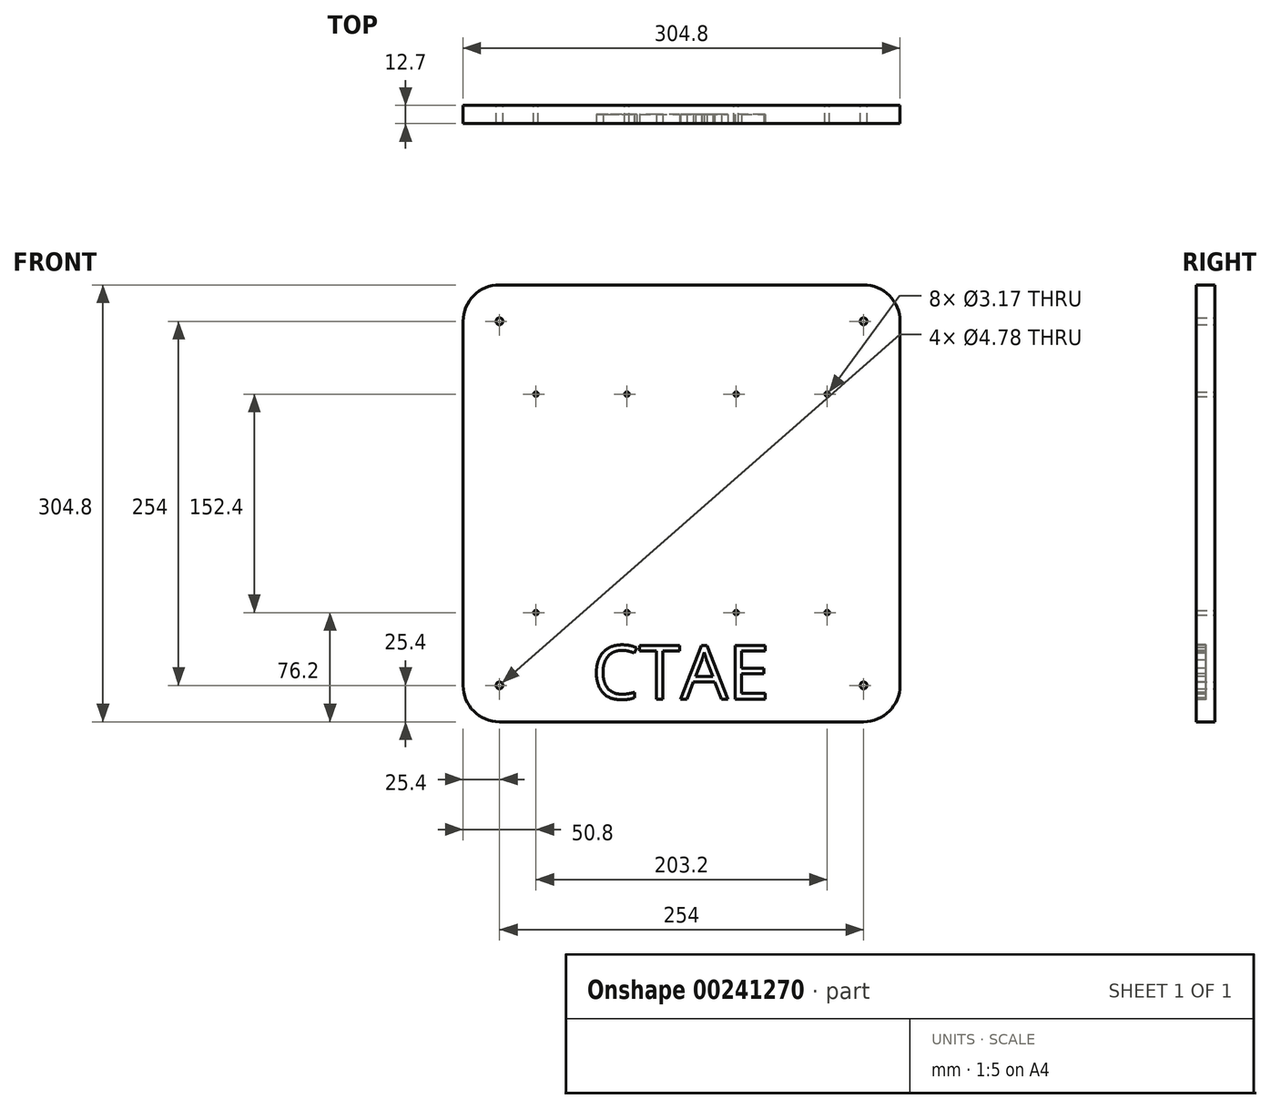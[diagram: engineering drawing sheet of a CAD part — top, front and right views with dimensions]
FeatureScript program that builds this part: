
annotation { "Feature Type Name" : "Feature", "Feature Type Description" : "" }
export const myFeature = defineFeature(function(context is Context, id is Id, definition is map)
    precondition{}
    {
        {
            var Q0;
            Q0=qCreatedBy(makeId("Front.planeOp"),FACE);
            var sketch = newSketch(context, id + "F0", { "sketchPlane" : qUnion([Q0])});
            skLineSegment(sketch, "E0.bottom", {"start": v(25.4, 0) * mm, "end": v(279.4, 0) * mm});
            skLineSegment(sketch, "E0.top", {"start": v(25.4, 304.8) * mm, "end": v(279.4, 304.8) * mm});
            skLineSegment(sketch, "E0.left", {"start": v(0, 25.4) * mm, "end": v(0, 279.4) * mm});
            skLineSegment(sketch, "E0.right", {"start": v(304.8, 25.4) * mm, "end": v(304.8, 279.4) * mm});
            skPoint(sketch, "E1.visualSharp", {"position": v(0, 304.8) * mm});
            skArc(sketch, "E1.filletArc", {"start": v(25.4, 304.8) * mm, "mid": v(7.44, 297.36) * mm, "end": v(0, 279.4) * mm});
            skPoint(sketch, "E2.visualSharp", {"position": v(304.8, 304.8) * mm});
            skArc(sketch, "E2.filletArc", {"start": v(304.8, 279.4) * mm, "mid": v(297.36, 297.36) * mm, "end": v(279.4, 304.8) * mm});
            skPoint(sketch, "E3.visualSharp", {"position": v(304.8, 0) * mm});
            skArc(sketch, "E3.filletArc", {"start": v(279.4, 0) * mm, "mid": v(297.36, 7.44) * mm, "end": v(304.8, 25.4) * mm});
            skPoint(sketch, "E4.visualSharp", {"position": v(0, 0) * mm});
            skArc(sketch, "E4.filletArc", {"start": v(0, 25.4) * mm, "mid": v(7.44, 7.44) * mm, "end": v(25.4, 0) * mm});
            skLineSegment(sketch, "E5", {"start": v(0, 152.4) * mm, "end": v(304.8, 152.4) * mm, "construction": true});
            skPoint(sketch, "E6", {"position": v(50.8, 228.6) * mm});
            skPoint(sketch, "E7", {"position": v(114.3, 228.6) * mm});
            skPoint(sketch, "E8", {"position": v(190.5, 228.6) * mm});
            skPoint(sketch, "E9", {"position": v(254, 228.6) * mm});
            skPoint(sketch, "E10.MirrorP", {"position": v(50.8, 76.2) * mm});
            skPoint(sketch, "E11.MirrorP", {"position": v(114.3, 76.2) * mm});
            skPoint(sketch, "E12.MirrorP", {"position": v(190.5, 76.2) * mm});
            skPoint(sketch, "E13.MirrorP", {"position": v(254, 76.2) * mm});
            skSolve(sketch);
        }
        {
            var Q0;
            Q0=makeQuery(id+"F0.imprint","IMPRINT",FACE,{"disambiguationData":[TD([[makeQuery(id+"F0.imprint","IMPRINT",EDGE,{"derivedFrom":sQuery(id+"F0.wireOp",EDGE,"E0.bottom")}),1.0]])]});
            extrude(context, id + "F1", {"entities" : qUnion([Q0]), "depth" : 12.7 * mm});
        }
        {
            var Q0;
            Q0=sQuery(id+"F0.wireOp",VERTEX,"E1.filletArc.center");
            var Q1;
            Q1=sQuery(id+"F0.wireOp",VERTEX,"E4.filletArc.center");
            var Q2;
            Q2=sQuery(id+"F0.wireOp",VERTEX,"E3.filletArc.center");
            var Q3;
            Q3=sQuery(id+"F0.wireOp",VERTEX,"E2.filletArc.center");
            var Q4;
            Q4=makeQuery(id+"F1.opExtrude","SWEPT_BODY",BODY,{"disambiguationData":[OSD([sQuery(id+"F0.wireOp",EDGE,"E0.bottom"),sQuery(id+"F0.wireOp",EDGE,"E0.top"),sQuery(id+"F0.wireOp",EDGE,"E0.left"),sQuery(id+"F0.wireOp",EDGE,"E0.right"),sQuery(id+"F0.wireOp",EDGE,"E1.filletArc"),sQuery(id+"F0.wireOp",EDGE,"E2.filletArc"),sQuery(id+"F0.wireOp",EDGE,"E3.filletArc"),sQuery(id+"F0.wireOp",EDGE,"E4.filletArc")])]});
            hole(context, id + "F2", {"style" : HoleStyle.SIMPLE, "endStyle" : HoleEndStyle.THROUGH, "oppositeDirection" : true, "holeDiameter" : 4.78 * mm, "locations" : qUnion([Q0, Q1, Q2, Q3]), "scope" : qUnion([Q4]), "isTappedThrough" : true});
        }
        {
            var Q0;
            Q0=sQuery(id+"F0.wireOp",VERTEX,"E6");
            var Q1;
            Q1=sQuery(id+"F0.wireOp",VERTEX,"E7");
            var Q2;
            Q2=sQuery(id+"F0.wireOp",VERTEX,"E8");
            var Q3;
            Q3=sQuery(id+"F0.wireOp",VERTEX,"E9");
            var Q4;
            Q4=sQuery(id+"F0.wireOp",VERTEX,"E13.MirrorP");
            var Q5;
            Q5=sQuery(id+"F0.wireOp",VERTEX,"E12.MirrorP");
            var Q6;
            Q6=sQuery(id+"F0.wireOp",VERTEX,"E10.MirrorP");
            var Q7;
            Q7=sQuery(id+"F0.wireOp",VERTEX,"E11.MirrorP");
            var Q8;
            Q8=makeQuery(id+"F1.opExtrude","SWEPT_BODY",BODY,{"disambiguationData":[OSD([sQuery(id+"F0.wireOp",EDGE,"E0.bottom"),sQuery(id+"F0.wireOp",EDGE,"E0.top"),sQuery(id+"F0.wireOp",EDGE,"E0.left"),sQuery(id+"F0.wireOp",EDGE,"E0.right"),sQuery(id+"F0.wireOp",EDGE,"E1.filletArc"),sQuery(id+"F0.wireOp",EDGE,"E2.filletArc"),sQuery(id+"F0.wireOp",EDGE,"E3.filletArc"),sQuery(id+"F0.wireOp",EDGE,"E4.filletArc")])]});
            hole(context, id + "F3", {"style" : HoleStyle.SIMPLE, "endStyle" : HoleEndStyle.THROUGH, "oppositeDirection" : true, "holeDiameter" : 3.17 * mm, "locations" : qUnion([Q0, Q1, Q2, Q3, Q4, Q5, Q6, Q7]), "scope" : qUnion([Q8]), "isTappedThrough" : true});
        }
        {
            var Q0;
            Q0=makeQuery(id+"F1.opExtrude","CAP_FACE",FACE,{"disambiguationData":[OSD([sQuery(id+"F0.wireOp",EDGE,"E0.bottom"),sQuery(id+"F0.wireOp",EDGE,"E0.top"),sQuery(id+"F0.wireOp",EDGE,"E0.left"),sQuery(id+"F0.wireOp",EDGE,"E0.right"),sQuery(id+"F0.wireOp",EDGE,"E1.filletArc"),sQuery(id+"F0.wireOp",EDGE,"E2.filletArc"),sQuery(id+"F0.wireOp",EDGE,"E3.filletArc"),sQuery(id+"F0.wireOp",EDGE,"E4.filletArc")])],"isStart":false});
            var sketch = newSketch(context, id + "F4", { "sketchPlane" : qUnion([Q0])});
            skText(sketch, "E14", { "text": "CTAE", "fontName": "OpenSans-Regular.ttf"});
            skLineSegment(sketch, "E15", {"start": v(152.4, 304.8) * mm, "end": v(152.4, -6.14) * mm, "construction": true});
            const initialGuessF4  = {"E14": [0.0898, 0.0159, 1, 0, 0.03762]};
            skSetInitialGuess(sketch, initialGuessF4);
            skSolve(sketch);
        }
        {
            var Q0;
            Q0 = qSketchRegion(id + "F4", true);
            extrude(context, id + "F5", {"entities" : qUnion([Q0]), "operationType" : NewBodyOperationType.REMOVE, "oppositeDirection" : true, "depth" : 6.35 * mm});
        }
    });
